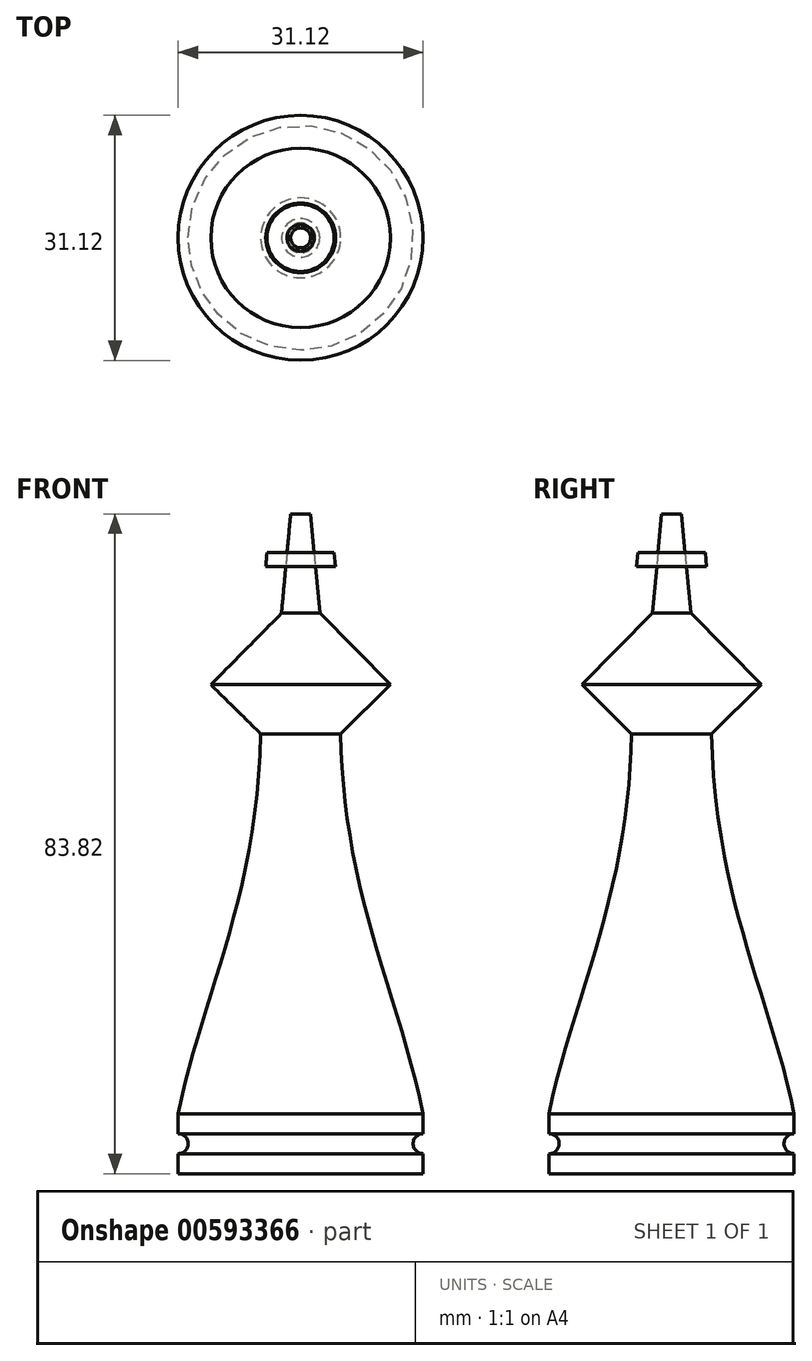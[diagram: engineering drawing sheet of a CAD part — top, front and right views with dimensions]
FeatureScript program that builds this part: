
annotation { "Feature Type Name" : "Feature", "Feature Type Description" : "" }
export const myFeature = defineFeature(function(context is Context, id is Id, definition is map)
    precondition{}
    {
        {
            var Q0;
            Q0=qCreatedBy(makeId("Front.planeOp"),FACE);
            var sketch = newSketch(context, id + "F0", { "sketchPlane" : qUnion([Q0])});
            skLineSegment(sketch, "E0", {"start": v(0, 0) * mm, "end": v(-12.7, 0) * mm});
            skLineSegment(sketch, "E1", {"start": v(-12.7, 0) * mm, "end": v(-12.7, 50.8) * mm});
            skLineSegment(sketch, "E2", {"start": v(-12.7, 50.8) * mm, "end": v(-5.08, 50.8) * mm});
            skLineSegment(sketch, "E3", {"start": v(-12.7, 0) * mm, "end": v(-12.7, 12.7) * mm});
            skLineSegment(sketch, "E4", {"start": v(-12.7, 12.7) * mm, "end": v(-2.54, 12.7) * mm});
            skFitSpline(sketch, "E5", {"points": [v(0, 0) * mm, v(-2.54, 12.7) * mm], "startDerivative": vector(22.35, 10) * mm, "endDerivative": vector(-0.02, 15.22) * mm});
            skFitSpline(sketch, "E6", {"points": [v(-2.54, 12.7) * mm, v(-5.08, 50.8) * mm], "startDerivative": vector(21.15, 41.24) * mm, "endDerivative": vector(28.6, 36.5) * mm});
            skLineSegment(sketch, "E7", {"start": v(-12.7, 50.8) * mm, "end": v(-12.7, 53.34) * mm});
            skLineSegment(sketch, "E8", {"start": v(-12.7, 53.34) * mm, "end": v(-5.08, 53.34) * mm});
            skFitSpline(sketch, "E9", {"points": [v(-5.08, 50.8) * mm, v(-5.08, 53.34) * mm], "startDerivative": vector(5.61, 0.48) * mm, "endDerivative": vector(-5.2, 0.4) * mm});
            skLineSegment(sketch, "E10", {"start": v(-5.08, 53.34) * mm, "end": v(-2.08, 59.7) * mm});
            skFitSpline(sketch, "E11", {"points": [v(-12.7, 53.34) * mm, v(-2.08, 59.7) * mm], "startDerivative": vector(12.15, 0) * mm, "endDerivative": vector(11.65, 0) * mm});
            skLineSegment(sketch, "E12", {"start": v(-12.7, 53.34) * mm, "end": v(-9.77, 53.34) * mm});
            skLineSegment(sketch, "E13.bottom", {"start": v(-12.7, 53.34) * mm, "end": v(-11.43, 53.34) * mm});
            skLineSegment(sketch, "E13.top", {"start": v(-12.7, 66.04) * mm, "end": v(-11.43, 66.04) * mm});
            skLineSegment(sketch, "E13.left", {"start": v(-12.7, 53.34) * mm, "end": v(-12.7, 66.04) * mm});
            skLineSegment(sketch, "E13.right", {"start": v(-11.43, 53.34) * mm, "end": v(-11.43, 66.04) * mm});
            skLineSegment(sketch, "E14.bottom", {"start": v(-12.7, 62.46) * mm, "end": v(-7.62, 62.46) * mm});
            skLineSegment(sketch, "E14.top", {"start": v(-12.7, 61.2) * mm, "end": v(-7.62, 61.2) * mm});
            skLineSegment(sketch, "E14.left", {"start": v(-12.7, 62.46) * mm, "end": v(-12.7, 61.2) * mm});
            skLineSegment(sketch, "E14.right", {"start": v(-7.62, 62.46) * mm, "end": v(-7.62, 61.2) * mm});
            skSolve(sketch);
        }
        {
            var Q0;
            Q0 = qSketchRegion(id + "F0", true);
            var Q1;
            Q1=sQuery(id+"F0.wireOp",EDGE,"E1");
            revolve(context, id + "F1", {"entities" : qUnion([Q0]), "axis" : qUnion([Q1]), "revolveType" : RevolveType.FULL});
        }
        {
            var Q0;
            Q0=makeQuery(id+"F1.opRevolve","SWEPT_BODY",BODY,{"disambiguationData":[OSD([sQuery(id+"F0.wireOp",EDGE,"E0"),sQuery(id+"F0.wireOp",EDGE,"E1"),sQuery(id+"F0.wireOp",EDGE,"E3"),sQuery(id+"F0.wireOp",EDGE,"E5"),sQuery(id+"F0.wireOp",EDGE,"E6"),sQuery(id+"F0.wireOp",EDGE,"E7"),sQuery(id+"F0.wireOp",EDGE,"E9"),sQuery(id+"F0.wireOp",EDGE,"E10"),sQuery(id+"F0.wireOp",EDGE,"E11"),sQuery(id+"F0.wireOp",EDGE,"E13.top"),sQuery(id+"F0.wireOp",EDGE,"E13.left"),sQuery(id+"F0.wireOp",EDGE,"E13.right"),sQuery(id+"F0.wireOp",EDGE,"E14.bottom"),sQuery(id+"F0.wireOp",EDGE,"E14.top"),sQuery(id+"F0.wireOp",EDGE,"E14.left"),sQuery(id+"F0.wireOp",EDGE,"E14.right")])]});
            deleteBodies(context, id + "F2", {"entities" : qUnion([Q0])});
        }
        {
            var Q0;
            Q0=qCreatedBy(makeId("Front.planeOp"),FACE);
            var sketch = newSketch(context, id + "F3", { "sketchPlane" : qUnion([Q0])});
            skLineSegment(sketch, "E15", {"start": v(0, 0) * mm, "end": v(-15.56, 0) * mm});
            skLineSegment(sketch, "E16", {"start": v(-15.56, 0) * mm, "end": v(-15.56, 2.54) * mm});
            skLineSegment(sketch, "E17", {"start": v(-15.56, 2.54) * mm, "end": v(-15.56, 5.08) * mm});
            skCircle(sketch, "E18", {"center": v(-15.56, 3.81) * mm, "radius": 1.27 * mm});
            skLineSegment(sketch, "E19", {"start": v(-15.56, 5.08) * mm, "end": v(-15.56, 7.62) * mm});
            skLineSegment(sketch, "E20", {"start": v(0, 0) * mm, "end": v(0, 55.88) * mm});
            skFitSpline(sketch, "E21", {"points": [v(-15.56, 7.62) * mm, v(-5.08, 55.88) * mm], "startDerivative": vector(9.22, 45.43) * mm, "endDerivative": vector(1.3, 62.47) * mm});
            skLineSegment(sketch, "E22", {"start": v(-5.08, 55.88) * mm, "end": v(0, 55.88) * mm});
            skLineSegment(sketch, "E23", {"start": v(0, 55.88) * mm, "end": v(0, 73.66) * mm});
            skLineSegment(sketch, "E24", {"start": v(-5.08, 55.88) * mm, "end": v(-11.4, 62.11) * mm});
            skLineSegment(sketch, "E25", {"start": v(-11.4, 62.11) * mm, "end": v(0, 73.66) * mm});
            skLineSegment(sketch, "E26", {"start": v(0, 70.02) * mm, "end": v(-2.54, 70.02) * mm});
            skLineSegment(sketch, "E27", {"start": v(0, 73.66) * mm, "end": v(0, 83.82) * mm});
            skLineSegment(sketch, "E28", {"start": v(0, 83.82) * mm, "end": v(-1.27, 83.82) * mm});
            skLineSegment(sketch, "E29", {"start": v(-1.27, 83.82) * mm, "end": v(-2.54, 70.02) * mm});
            skLineSegment(sketch, "E30.0", {"start": v(-3.8, 84.05) * mm, "end": v(-5.07, 70.25) * mm});
            skLineSegment(sketch, "E31", {"start": v(-4.43, 77.15) * mm, "end": v(0, 77.15) * mm});
            skPoint(sketch, "E31.endSnap0", {"position": v(-4.43, 77.15) * mm});
            skLineSegment(sketch, "E32", {"start": v(0, 77.15) * mm, "end": v(0, 78.3) * mm});
            skLineSegment(sketch, "E33.0", {"start": v(-4.43, 78.93) * mm, "end": v(0, 78.93) * mm});
            skSolve(sketch);
        }
        {
            var Q0;
            {var subQ0=sQuery(id+"F3.wireOp",EDGE,"E28");Q0=makeQuery(id+"F3.imprint","IMPRINT",FACE,{"disambiguationData":[TD([[makeQuery(id+"F3.imprint","IMPRINT",EDGE,{"derivedFrom":subQ0}),1.0]])]});}
            var Q1;
            {var subQ0=sQuery(id+"F3.wireOp",EDGE,"E33.0");var subQ1=sQuery(id+"F3.wireOp",EDGE,"E29");var subQ2=makeQuery(id+"F3.imprint","INTERSECT",VERTEX,{"derivedFrom":[subQ1,subQ0]});Q1=makeQuery(id+"F3.imprint","IMPRINT",FACE,{"disambiguationData":[TD([[makeQuery(id+"F3.imprint","IMPRINT",EDGE,{"disambiguationData":[TD([[subQ2,-1.0]])],"derivedFrom":subQ1}),-1.0]])]});}
            var Q2;
            Q2=makeQuery(id+"F3.imprint","IMPRINT",FACE,{"disambiguationData":[TD([[makeQuery(id+"F3.imprint","IMPRINT",EDGE,{"derivedFrom":sQuery(id+"F3.wireOp",EDGE,"E15")}),-1.0]])]});
            var Q3;
            {var subQ6=sQuery(id+"F3.wireOp",EDGE,"E22");Q3=makeQuery(id+"F3.imprint","IMPRINT",FACE,{"disambiguationData":[TD([[makeQuery(id+"F3.imprint","IMPRINT",EDGE,{"derivedFrom":subQ6}),1.0]])]});}
            var Q4;
            {var subQ3=sQuery(id+"F3.wireOp",EDGE,"E26");Q4=makeQuery(id+"F3.imprint","IMPRINT",FACE,{"disambiguationData":[TD([[makeQuery(id+"F3.imprint","IMPRINT",EDGE,{"derivedFrom":subQ3}),-1.0]])]});}
            var Q5;
            {var subQ1=sQuery(id+"F3.wireOp",EDGE,"E25");var subQ3=sQuery(id+"F3.wireOp",EDGE,"E29");var subQ4=makeQuery(id+"F3.imprint","INTERSECT",VERTEX,{"derivedFrom":[subQ1,subQ3]});Q5=makeQuery(id+"F3.imprint","IMPRINT",FACE,{"disambiguationData":[TD([[makeQuery(id+"F3.imprint","IMPRINT",EDGE,{"disambiguationData":[TD([[subQ4,1.0]])],"derivedFrom":subQ3}),1.0]])]});}
            var Q6;
            {var subQ0=sQuery(id+"F3.wireOp",EDGE,"E32");Q6=makeQuery(id+"F3.imprint","IMPRINT",FACE,{"disambiguationData":[TD([[makeQuery(id+"F3.imprint","IMPRINT",EDGE,{"derivedFrom":subQ0}),1.0]])]});}
            var Q7;
            Q7=sQuery(id+"F3.wireOp",EDGE,"E20");
            revolve(context, id + "F4", {"entities" : qUnion([Q0, Q1, Q2, Q3, Q4, Q5, Q6]), "axis" : qUnion([Q7]), "revolveType" : RevolveType.FULL});
        }
    });
